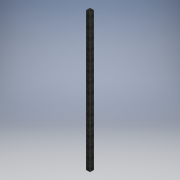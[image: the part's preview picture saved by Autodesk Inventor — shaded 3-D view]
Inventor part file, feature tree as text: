
AUTODESK INVENTOR PART (.ipt)
format: ipt  version: 2018 (Build 220112000, 112)  size: 112,128 bytes
history: native  units: mm
features: other x1, extrude x1, fillet x1, sketch x1
ambient origin geometry x8: Origin, YZ Plane, XZ Plane, XY Plane, X Axis, Y Axis, Z Axis, Center Point
bodies: Body1 (feature_tree)
feature tree (4):
  other  "Sólido1"
  extrude  "Extrusión1"  Depth=75.0mm
  fillet  "Empalme1"  Radius=3.0mm
  sketch  "Boceto1"  dims[d0=75.0mm d1=75.0mm d2=3.0mm d3=2570.0mm d4=0.0mm d5=6.0mm]
